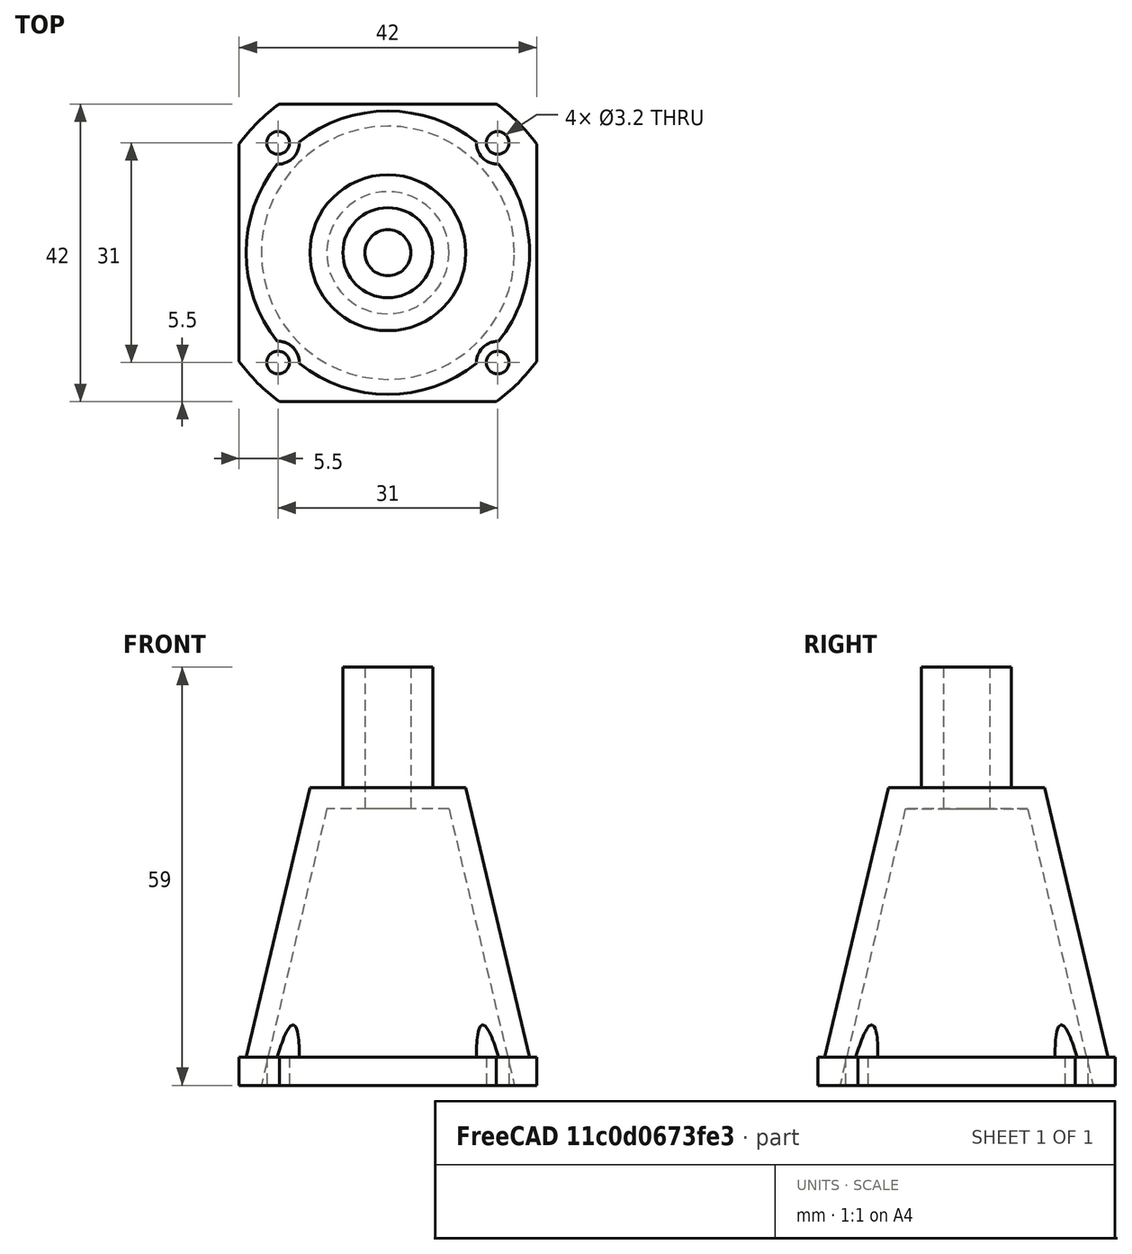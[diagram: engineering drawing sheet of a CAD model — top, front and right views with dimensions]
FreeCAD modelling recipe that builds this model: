
FCSTD DOCUMENT  (FreeCAD 0.19R23578 (Git))
Label: bell_housing
License: All rights reserved
LicenseURL: http://en.wikipedia.org/wiki/All_rights_reserved
objects: Sketcher::SketchObject×3, PartDesign::LinearPattern×2, Mesh::Feature×1, PartDesign::Revolution×1, PartDesign::Pocket×1, PartDesign::PolarPattern×1, PartDesign::Groove×1, PartDesign::MultiTransform×1, PartDesign::Body×1
note: 14 computed .brp shape members not serialized (recipe doc carries the construction recipe); baked Part::Feature solids carry a one-line shape summary decoded from their .brp

FEATURE [Mesh::Feature] MotorCap
  Placement = pos=(-64.5,80.2,-1.1) rot=(0,0,1;0rad)
FEATURE [Sketcher::SketchObject] Sketch
  MapMode = 5
  Placement = pos=(0,0,0) rot=(1,0,0;1.5708rad)
  Support = -> [XZ_Plane]
  sketch-geometry (12):
    g0: LineSegment StartX=26 StartY=0 StartZ=0 EndX=26 EndY=4 EndZ=0
    g1: LineSegment StartX=26 StartY=4 StartZ=0 EndX=20 EndY=4 EndZ=0
    g2: LineSegment StartX=20 StartY=4 StartZ=0 EndX=11 EndY=42 EndZ=0
    g3: LineSegment StartX=11 StartY=42 StartZ=0 EndX=6.35 EndY=42 EndZ=0
    g4: LineSegment StartX=6.35 StartY=42 StartZ=0 EndX=6.35 EndY=59 EndZ=0
    g5: LineSegment StartX=6.35 StartY=59 StartZ=0 EndX=3.25 EndY=59 EndZ=0
    g6: LineSegment StartX=17.8644 StartY=0 StartZ=0 EndX=26 EndY=0 EndZ=0
    g7: LineSegment StartX=3.25 StartY=59 StartZ=0 EndX=3.25 EndY=39 EndZ=0
    g8: LineSegment StartX=3.25 StartY=39 StartZ=0 EndX=8.62753 EndY=39 EndZ=0
    g9: LineSegment StartX=8.62753 StartY=39 StartZ=0 EndX=17.8644 EndY=0 EndZ=0
    g10: GeomPoint X=17.0808 Y=3.3086 Z=0
    g11: LineSegment StartX=17.0808 StartY=3.3086 StartZ=0 EndX=20 EndY=4 EndZ=0
  constraints (34):
    c: PointOnObject(g0,g-1)
    c: Vertical(g0)
    c: Coincident(g0,g1)
    c: Horizontal(g1)
    c: Coincident(g1,g2)
    c: Coincident(g2,g3)
    c: Horizontal(g3)
    c: Coincident(g3,g4)
    c: Vertical(g4)
    c: Coincident(g4,g5)
    c: Horizontal(g5)
    c: Coincident(g6,g0)
    c: DistanceY(g0,g0) = 4
    c: DistanceX(g-1,g6) = 26
    c: DistanceX(g-1,g2) = 11
    c: DistanceY(g-1,g2) = 42
    c: DistanceX(g-1,g1) = 20
    c: Vertical(g7)
    c: Coincident(g7,g8)
    c: Horizontal(g8)
    c: Coincident(g8,g9)
    c: Coincident(g6,g9)
    c: Coincident(g5,g7)
    c: DistanceX(g-1,g4) = 6.35
    c: DistanceY(g8,g3) = 3
    c: Parallel(g9,g2)
    c: Horizontal(g6)
    c: PointOnObject(g10,g9)
    c: Coincident(g11,g10)
    c: Coincident(g11,g1)
    c: Perpendicular(g9,g11)
    c: Distance(g11) = 3
    c: DistanceY(g-1,g5) = 59
    c: DistanceX(g-1,g5) = 3.25
FEATURE [PartDesign::Revolution] Revolution
  Angle = 360
  Axis = (-3e-16,3e-16,1)
  Base = (0,0,0)
  Placement = pos=(0,0,0) rot=(1,0,0;1.5708rad)
  Profile = -> Sketch
  ReferenceAxis = -> Z_Axis
  Reversed = true
FEATURE [Sketcher::SketchObject] Sketch001
  MapMode = 5
  Support = -> [XY_Plane]
  sketch-geometry (4):
    g0: LineSegment StartX=-25 StartY=21 StartZ=0 EndX=25 EndY=21 EndZ=0
    g1: LineSegment StartX=25 StartY=21 StartZ=0 EndX=25 EndY=41 EndZ=0
    g2: LineSegment StartX=25 StartY=41 StartZ=0 EndX=-25 EndY=41 EndZ=0
    g3: LineSegment StartX=-25 StartY=41 StartZ=0 EndX=-25 EndY=21 EndZ=0
  constraints (11):
    c: Coincident(g0,g1)
    c: Coincident(g1,g2)
    c: Coincident(g2,g3)
    c: Coincident(g3,g0)
    c: Horizontal(g2)
    c: Vertical(g1)
    c: Vertical(g3)
    c: DistanceY(g1,g1) = 20
    c: DistanceX(g0,g0) = 50
    c: Symmetric(g0,g0,g-2)
    c: DistanceY(g-1,g0) = 21
FEATURE [PartDesign::Pocket] Pocket
  BaseFeature = -> Revolution
  Length = 5
  Length2 = 100
  Midplane = true
  Placement = pos=(0,0,0) rot=(1,0,0;1.5708rad)
  Profile = -> Sketch001
  Type = 1
FEATURE [PartDesign::PolarPattern] PolarPattern
  Angle = 360
  Axis = -> Sketch001 [N_Axis]
  BaseFeature = -> Pocket
  Occurrences = 4
  Originals = -> [Pocket]
  Placement = pos=(0,0,0) rot=(1,0,0;1.5708rad)
FEATURE [Sketcher::SketchObject] Sketch002
  AttachmentOffset = pos=(15.5,4,15.5) rot=(0,0,1;0rad)
  MapMode = 5
  Placement = pos=(15.5,-15.5,4) rot=(1,0,0;1.5708rad)
  Support = -> [XZ_Plane]
  sketch-geometry (6):
    g0: LineSegment StartX=0 StartY=10 StartZ=0 EndX=3 EndY=10 EndZ=0
    g1: LineSegment StartX=3 StartY=10 StartZ=0 EndX=3 EndY=0 EndZ=0
    g2: LineSegment StartX=3 StartY=0 StartZ=0 EndX=1.6 EndY=0 EndZ=0
    g3: LineSegment StartX=1.6 StartY=0 StartZ=0 EndX=1.6 EndY=-10 EndZ=0
    g4: LineSegment StartX=1.6 StartY=-10 StartZ=0 EndX=0 EndY=-10 EndZ=0
    g5: LineSegment StartX=0 StartY=-10 StartZ=0 EndX=0 EndY=10 EndZ=0
  constraints (18):
    c: PointOnObject(g0,g-2)
    c: Horizontal(g0)
    c: Coincident(g0,g1)
    c: Vertical(g1)
    c: Coincident(g1,g2)
    c: Horizontal(g2)
    c: Coincident(g2,g3)
    c: Vertical(g3)
    c: Coincident(g3,g4)
    c: PointOnObject(g4,g-2)
    c: Coincident(g4,g5)
    c: Coincident(g5,g0)
    c: Horizontal(g4)
    c: DistanceX(g0,g0) = 3
    c: DistanceX(g4,g4) = 1.6
    c: DistanceY(g3,g3) = 10
    c: PointOnObject(g1,g-1)
    c: DistanceY(g1,g1) = 10
FEATURE [PartDesign::Groove] Groove
  Angle = 360
  Axis = (0,2e-16,1)
  Base = (15.5,-15.5,4)
  BaseFeature = -> PolarPattern
  Placement = pos=(0,0,0) rot=(1,0,0;1.5708rad)
  Profile = -> Sketch002
  ReferenceAxis = -> Sketch002 [V_Axis]
FEATURE [PartDesign::LinearPattern] LinearPattern
  Direction = -> Sketch002 [H_Axis]
  Length = 31
  Occurrences = 2
  Placement = pos=(0,0,0) rot=(1,0,0;1.5708rad)
  Reversed = true
FEATURE [PartDesign::LinearPattern] LinearPattern001
  Direction = -> Y_Axis
  Length = 31
  Occurrences = 2
  Placement = pos=(0,0,0) rot=(1,0,0;1.5708rad)
FEATURE [PartDesign::MultiTransform] MultiTransform
  BaseFeature = -> Groove
  Originals = -> [Groove]
  Placement = pos=(0,0,0) rot=(1,0,0;1.5708rad)
  Transformations = -> [LinearPattern,LinearPattern001]
FEATURE [PartDesign::Body] Body
  Group = -> [Sketch,Revolution,Sketch001,Pocket,PolarPattern,Sketch002,Groove,MultiTransform,LinearPattern,LinearPattern001]
  Origin = -> Origin
  Tip = -> MultiTransform
